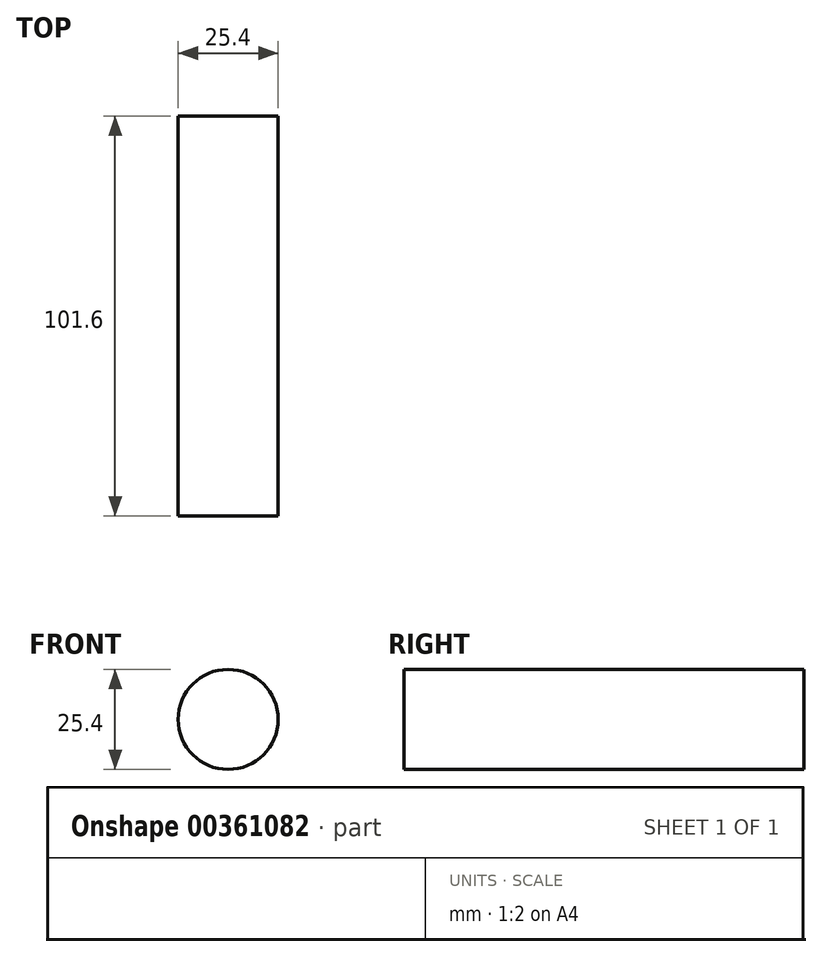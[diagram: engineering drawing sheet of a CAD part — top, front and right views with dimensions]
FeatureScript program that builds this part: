
annotation { "Feature Type Name" : "Feature", "Feature Type Description" : "" }
export const myFeature = defineFeature(function(context is Context, id is Id, definition is map)
    precondition{}
    {
        {
            var Q0;
            Q0=qCreatedBy(makeId("Front.planeOp"),FACE);
            var sketch = newSketch(context, id + "F0", { "sketchPlane" : qUnion([Q0])});
            skCircle(sketch, "E0", {"center": v(33.4, -41.9) * mm, "radius": 12.7 * mm});
            skSolve(sketch);
        }
        {
            var Q0;
            Q0=makeQuery(id+"F0.imprint","IMPRINT",FACE,{"disambiguationData":[TD([[makeQuery(id+"F0.imprint","IMPRINT",EDGE,{"derivedFrom":sQuery(id+"F0.wireOp",EDGE,"E0")}),1.0]])]});
            var Q1;
            Q1 = qSketchRegion(id + "F0", true);
            extrude(context, id + "F1", {"entities" : qUnion([Q0, Q1]), "depth" : 101.6 * mm});
        }
    });
